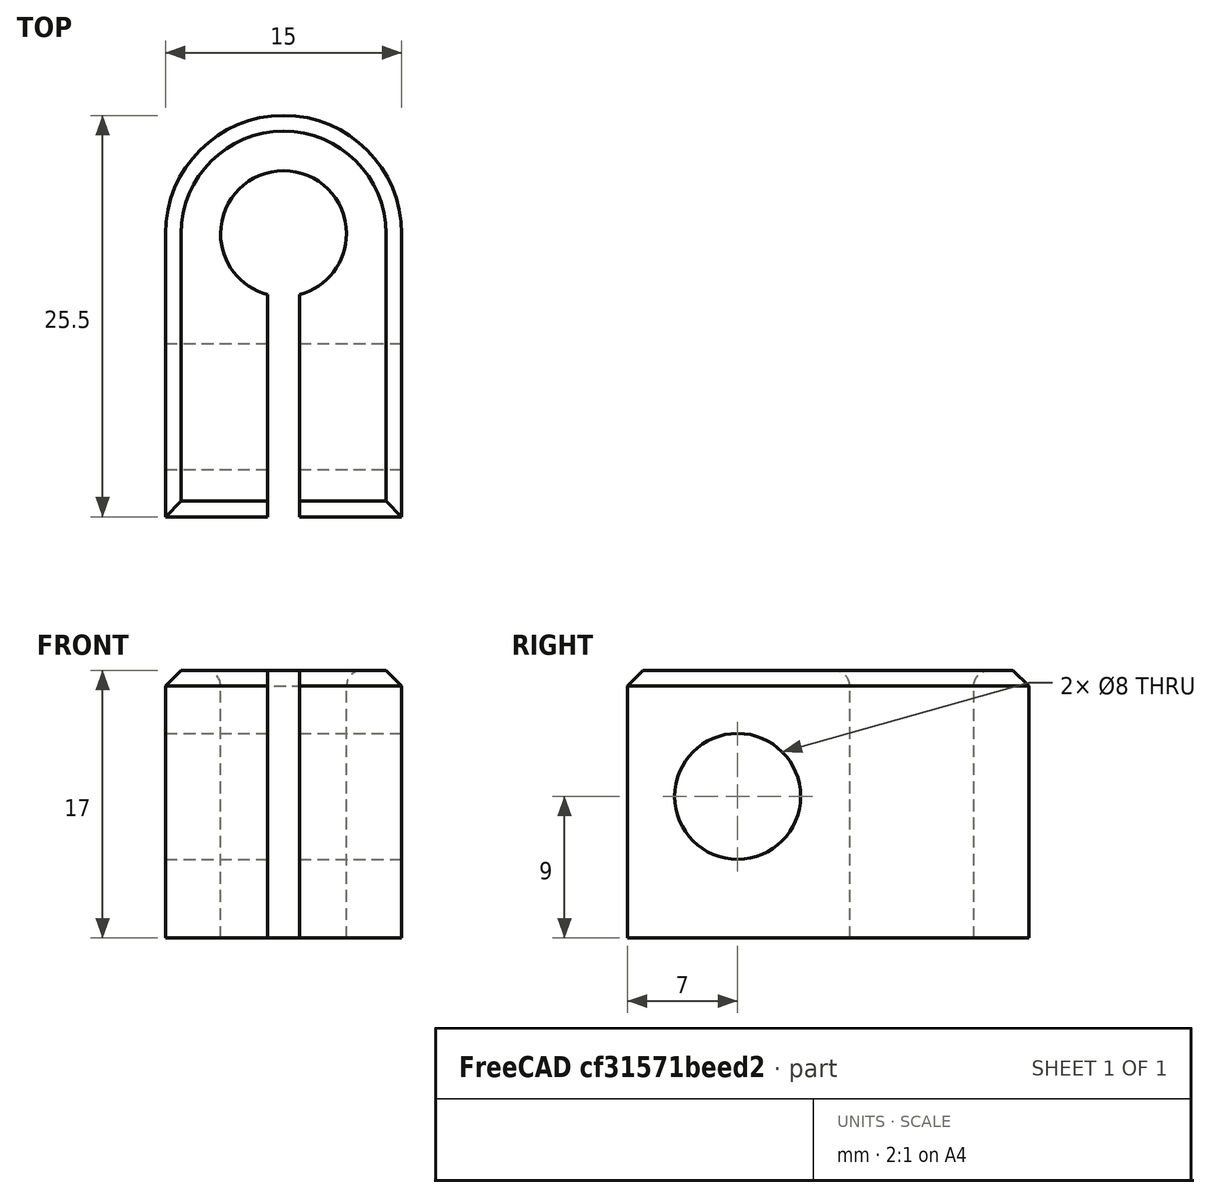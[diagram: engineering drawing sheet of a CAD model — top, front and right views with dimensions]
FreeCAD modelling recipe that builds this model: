
FCSTD DOCUMENT  (FreeCAD 0.16R6706 (Git))
Label: FC3
License: All rights reserved
LicenseURL: http://en.wikipedia.org/wiki/All_rights_reserved
objects: Part::Cylinder×3, Part::Cut×3, Part::Box×2, Part::MultiFuse×1, Part::Chamfer×1, Part::Fillet×1
note: 11 computed .brp shape members not serialized (recipe doc carries the construction recipe); baked Part::Feature solids carry a one-line shape summary decoded from their .brp

FEATURE [Part::Box] Box  label="Куб"
  Height = 17
  Length = 15
  Width = 18
FEATURE [Part::Cylinder] Cylinder  label="Цилиндр"
  Angle = 360
  Height = 17
  Placement = pos=(7.5,18,0) rot=(0,0,1;0rad)
  Radius = 7.5
FEATURE [Part::MultiFuse] Fusion
  Shapes = -> [Cylinder,Box]
FEATURE [Part::Cylinder] Cylinder001  label="Цилиндр001"
  Angle = 360
  Height = 17
  Placement = pos=(7.5,18,0) rot=(0,0,1;0rad)
  Radius = 4
FEATURE [Part::Cut] Cut
  Base = -> Fusion
  Tool = -> Cylinder001
FEATURE [Part::Cylinder] Cylinder002  label="Цилиндр002"
  Angle = 360
  Height = 15
  Placement = pos=(0,7,9) rot=(0,1,0;1.5708rad)
  Radius = 4
FEATURE [Part::Cut] Cut001
  Base = -> Cut
  Tool = -> Cylinder002
FEATURE [Part::Box] Box001  label="Куб001"
  Height = 17
  Length = 2
  Placement = pos=(6.5,0,0) rot=(0,0,1;0rad)
  Width = 17
FEATURE [Part::Cut] Cut002
  Base = -> Cut001
  Tool = -> Box001
FEATURE [Part::Chamfer] Chamfer
  Base = -> Cut002
  Edges = 5 edges r=1: [Edge3,Edge14,Edge25,Edge34,Edge46]
FEATURE [Part::Fillet] Fillet
  Base = -> Chamfer
  Edges = 3 edges r=1: [Edge24,Edge25,Edge41]
